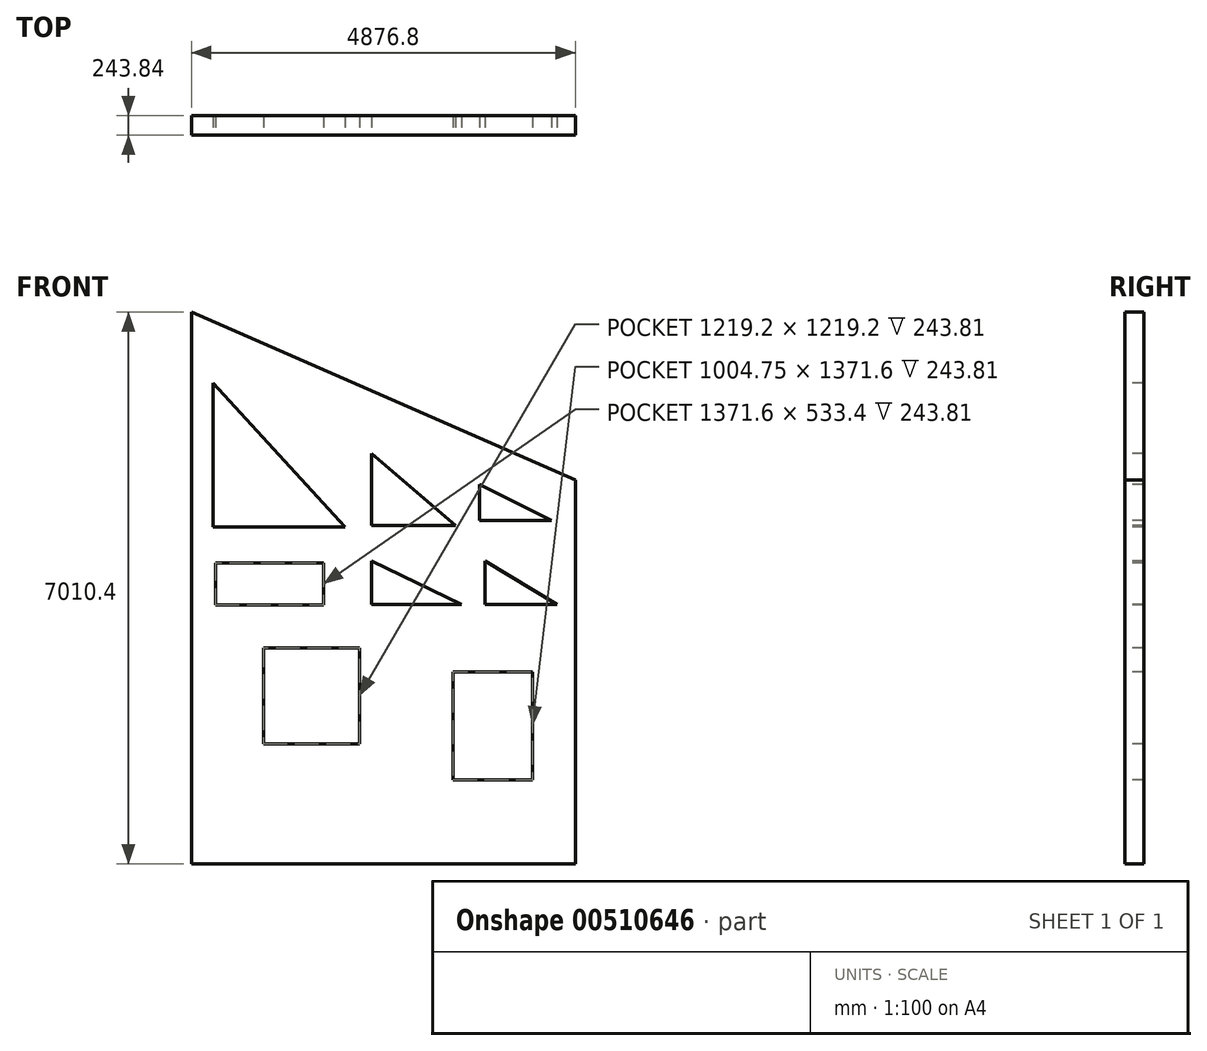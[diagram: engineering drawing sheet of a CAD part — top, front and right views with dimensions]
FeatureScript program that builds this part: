
annotation { "Feature Type Name" : "Feature", "Feature Type Description" : "" }
export const myFeature = defineFeature(function(context is Context, id is Id, definition is map)
    precondition{}
    {
        {
            var Q0;
            Q0=qCreatedBy(makeId("Front.planeOp"),FACE);
            var sketch = newSketch(context, id + "F0", { "sketchPlane" : qUnion([Q0])});
            skLineSegment(sketch, "E0", {"start": v(-5046.09, 3324) * mm, "end": v(-5046.09, -3686.4) * mm});
            skLineSegment(sketch, "E1", {"start": v(-5046.09, -3686.4) * mm, "end": v(-169.29, -3686.4) * mm});
            skLineSegment(sketch, "E2", {"start": v(-169.29, -3686.4) * mm, "end": v(-169.29, 1190.4) * mm});
            skLineSegment(sketch, "E3", {"start": v(-169.29, 1190.4) * mm, "end": v(-5046.09, 3324) * mm});
            skSolve(sketch);
        }
        {
            var Q0;
            Q0 = qSketchRegion(id + "F0", true);
            extrude(context, id + "F1", {"entities" : qUnion([Q0]), "depth" : 243.84 * mm, "offsetDistance" : 30.48 * mm});
        }
        {
            var Q0;
            Q0=makeQuery(id+"F1.opExtrude","CAP_FACE",FACE,{"disambiguationData":[OSD([sQuery(id+"F0.wireOp",EDGE,"E0"),sQuery(id+"F0.wireOp",EDGE,"E1"),sQuery(id+"F0.wireOp",EDGE,"E2"),sQuery(id+"F0.wireOp",EDGE,"E3")])],"isStart":false});
            var sketch = newSketch(context, id + "F2", { "sketchPlane" : qUnion([Q0])});
            skLineSegment(sketch, "E4", {"start": v(-4772.39, 2420.41) * mm, "end": v(-4772.39, 591.61) * mm});
            skLineSegment(sketch, "E5", {"start": v(-4772.39, 591.61) * mm, "end": v(-3095.99, 591.61) * mm});
            skLineSegment(sketch, "E6", {"start": v(-3095.99, 591.61) * mm, "end": v(-4772.39, 2420.41) * mm});
            skLineSegment(sketch, "E7", {"start": v(-2758.4, 1529.16) * mm, "end": v(-2758.4, 614.76) * mm});
            skLineSegment(sketch, "E8", {"start": v(-2758.4, 614.76) * mm, "end": v(-1691.6, 614.76) * mm});
            skLineSegment(sketch, "E9", {"start": v(-1691.6, 614.76) * mm, "end": v(-2758.4, 1529.16) * mm});
            skLineSegment(sketch, "E10", {"start": v(-1388.49, 1135.62) * mm, "end": v(-1388.49, 678.42) * mm});
            skLineSegment(sketch, "E11", {"start": v(-1388.49, 678.42) * mm, "end": v(-474.09, 678.42) * mm});
            skLineSegment(sketch, "E12", {"start": v(-474.09, 678.42) * mm, "end": v(-1388.49, 1135.62) * mm});
            skLineSegment(sketch, "E13", {"start": v(-4741.29, 134.41) * mm, "end": v(-3369.69, 134.41) * mm});
            skLineSegment(sketch, "E14", {"start": v(-3369.69, 134.41) * mm, "end": v(-3369.69, -398.99) * mm});
            skLineSegment(sketch, "E15", {"start": v(-3369.69, -398.99) * mm, "end": v(-4741.29, -398.99) * mm});
            skLineSegment(sketch, "E16", {"start": v(-4741.29, -398.99) * mm, "end": v(-4741.29, 134.41) * mm});
            skLineSegment(sketch, "E17", {"start": v(-2757.97, 162.7) * mm, "end": v(-2757.97, -394.29) * mm});
            skLineSegment(sketch, "E18", {"start": v(-2757.97, -394.29) * mm, "end": v(-1614.97, -394.29) * mm});
            skLineSegment(sketch, "E19", {"start": v(-1614.97, -394.29) * mm, "end": v(-2757.97, 162.7) * mm});
            skLineSegment(sketch, "E20", {"start": v(-1316.37, 162.7) * mm, "end": v(-1316.37, -394.29) * mm});
            skLineSegment(sketch, "E21", {"start": v(-1316.37, -394.29) * mm, "end": v(-401.97, -394.29) * mm});
            skLineSegment(sketch, "E22", {"start": v(-401.97, -394.29) * mm, "end": v(-1316.37, 162.7) * mm});
            skLineSegment(sketch, "E23.bottom", {"start": v(-4131.69, -943.2) * mm, "end": v(-2912.49, -943.2) * mm});
            skLineSegment(sketch, "E23.top", {"start": v(-4131.69, -2162.4) * mm, "end": v(-2912.49, -2162.4) * mm});
            skLineSegment(sketch, "E23.left", {"start": v(-4131.69, -943.2) * mm, "end": v(-4131.69, -2162.4) * mm});
            skLineSegment(sketch, "E23.right", {"start": v(-2912.49, -943.2) * mm, "end": v(-2912.49, -2162.4) * mm});
            skLineSegment(sketch, "E24.bottom", {"start": v(-1720.46, -1248) * mm, "end": v(-715.7, -1248) * mm});
            skLineSegment(sketch, "E24.top", {"start": v(-1720.46, -2619.6) * mm, "end": v(-715.7, -2619.6) * mm});
            skLineSegment(sketch, "E24.left", {"start": v(-1720.46, -1248) * mm, "end": v(-1720.46, -2619.6) * mm});
            skLineSegment(sketch, "E24.right", {"start": v(-715.7, -1248) * mm, "end": v(-715.7, -2619.6) * mm});
            skSolve(sketch);
        }
        {
            var Q0;
            Q0 = qSketchRegion(id + "F2", true);
            extrude(context, id + "F3", {"entities" : qUnion([Q0]), "operationType" : NewBodyOperationType.REMOVE, "oppositeDirection" : true, "depth" : 243.8 * mm, "offsetDistance" : 30.48 * mm});
        }
    });
